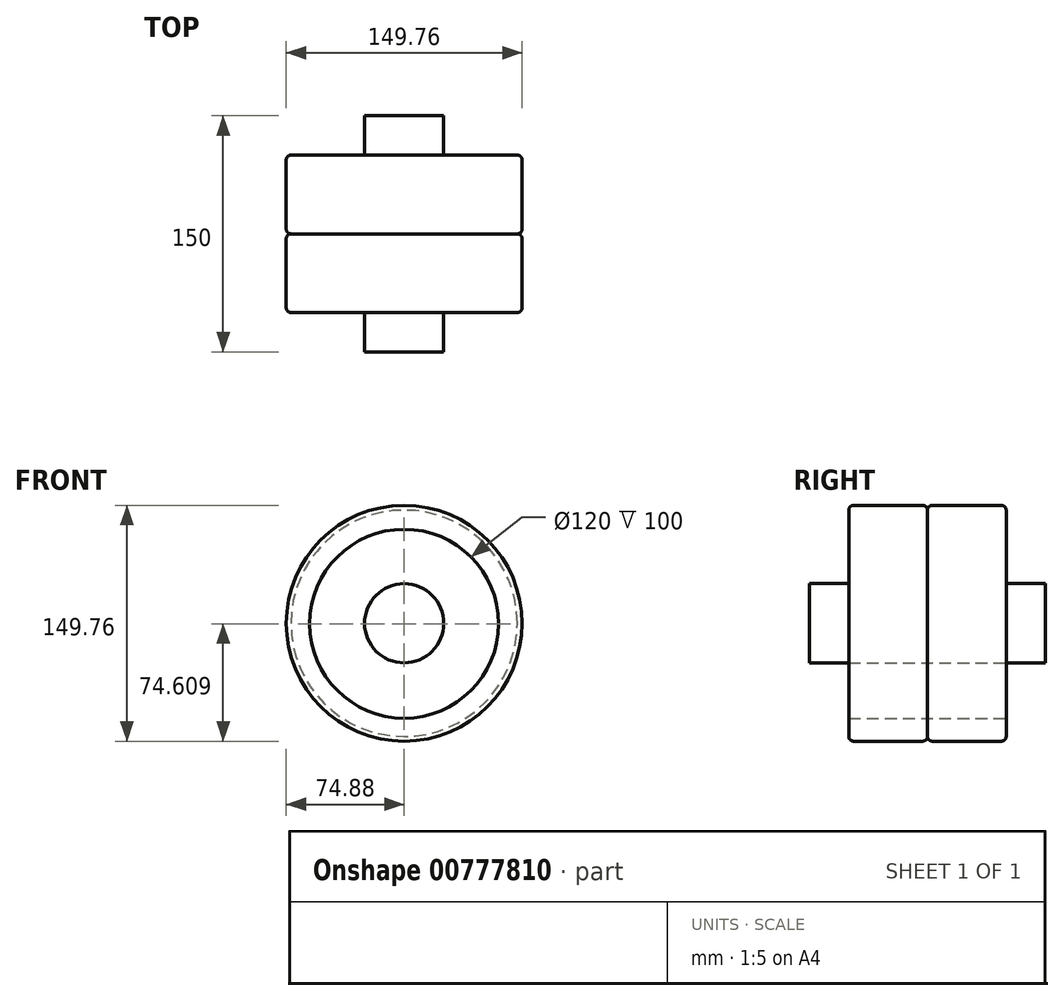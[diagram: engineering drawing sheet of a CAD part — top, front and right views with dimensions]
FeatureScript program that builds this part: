
annotation { "Feature Type Name" : "Feature", "Feature Type Description" : "" }
export const myFeature = defineFeature(function(context is Context, id is Id, definition is map)
    precondition{}
    {
        {
            var Q0;
            Q0=qCreatedBy(makeId("Front.planeOp"),FACE);
            var sketch = newSketch(context, id + "F0", { "sketchPlane" : qUnion([Q0])});
            skCircle(sketch, "E0", {"center": v(0, 0) * mm, "radius": 74.88 * mm});
            skSolve(sketch);
        }
        {
            var Q0;
            Q0=makeQuery(id+"F0.imprint","IMPRINT",FACE,{"disambiguationData":[TD([[makeQuery(id+"F0.imprint","IMPRINT",EDGE,{"derivedFrom":sQuery(id+"F0.wireOp",EDGE,"E0")}),1.0]])]});
            var Q1;
            Q1=sQuery(id+"F0.wireOp",EDGE,"E0");
            extrude(context, id + "F1", {"entities" : qUnion([Q0]), "surfaceEntities" : qUnion([Q1]), "depth" : 50 * mm, "offsetDistance" : 25 * mm});
        }
        {
            var Q0;
            Q0=qCreatedBy(makeId("Front.planeOp"),FACE);
            var sketch = newSketch(context, id + "F2", { "sketchPlane" : qUnion([Q0])});
            skCircle(sketch, "E1", {"center": v(0, -0.27) * mm, "radius": 52.36 * mm});
            skSolve(sketch);
        }
        {
            var Q0;
            Q0=sQuery(id+"F2.wireOp",VERTEX,"E1.center");
            var Q1;
            Q1=makeQuery(id+"F1.opExtrude","SWEPT_BODY",BODY,{"disambiguationData":[OSD([sQuery(id+"F0.wireOp",EDGE,"E0")])]});
            hole(context, id + "F3", {"style" : HoleStyle.SIMPLE, "endStyle" : HoleEndStyle.THROUGH, "oppositeDirection" : true, "holeDiameter" : 120 * mm, "majorDiameter" : 5 * mm, "isTappedThrough" : true, "tappedDepth" : 12 * mm, "tapClearance" : 3, "locations" : qUnion([Q0]), "scope" : qUnion([Q1])});
        }
        {
            var Q0;
            Q0=makeQuery(id+"F1.opExtrude","CAP_EDGE",EDGE,{"disambiguationData":[OSD([sQuery(id+"F0.wireOp",EDGE,"E0")])],"isStart":false});
            var Q1;
            Q1=makeQuery(id+"F1.opExtrude","CAP_EDGE",EDGE,{"disambiguationData":[OSD([sQuery(id+"F0.wireOp",EDGE,"E0")])],"isStart":true});
            fillet(context, id + "F4", {"entities" : qUnion([Q0, Q1]), "radius" : 3 * mm, "tangentPropagation" : true, "allowEdgeOverflow" : false});
        }
        {
            var Q0;
            Q0=makeQuery(id+"F1.opExtrude","SWEPT_BODY",BODY,{"disambiguationData":[OSD([sQuery(id+"F0.wireOp",EDGE,"E0")])]});
            var Q1;
            Q1=qCreatedBy(makeId("Front.planeOp"),FACE);
            mirror(context, id + "F5", {"operationType" : NewBodyOperationType.ADD, "entities" : qUnion([Q0]), "mirrorPlane" : qUnion([Q1])});
        }
        {
            var Q0;
            Q0=qCreatedBy(makeId("Front.planeOp"),FACE);
            var sketch = newSketch(context, id + "F6", { "sketchPlane" : qUnion([Q0])});
            skCircle(sketch, "E2", {"center": v(0, 0) * mm, "radius": 25.16 * mm});
            skSolve(sketch);
        }
        {
            var Q0;
            Q0=makeQuery(id+"F6.imprint","IMPRINT",FACE,{"disambiguationData":[TD([[makeQuery(id+"F6.imprint","IMPRINT",EDGE,{"derivedFrom":sQuery(id+"F6.wireOp",EDGE,"E2")}),1.0]])]});
            extrude(context, id + "F7", {"entities" : qUnion([Q0]), "endBound" : BoundingType.SYMMETRIC, "depth" : 150 * mm, "offsetDistance" : 25 * mm});
        }
    });
